# Revit family: Shower_Set-DXV-Modulus-D35120780_Series
name_source: partatom
category: Plumbing Fixtures
revit_build: Autodesk Revit 2018 (Build: 20170223_1515(x64)
units: mm (PartAtom-declared; Revit-internal decimal feet)

## family parameters
Cut with Voids When Loaded = No
Host = Face
OmniClass Number = 23.45.05.14.17
OmniClass Title = Showers
Part Type = Normal
Room Calculation Point = No
Round Connector Dimension = Use Diameter
Shared = Yes

## types (4) — shared parameters
Assembly Code = D2010710
CEC Compliant = Yes
CW Connection = Yes
CWFU = 3
CalGreen Compliant = Yes
Connection Size = 1/2"
Default Elevation = 0"
Description = DXV Modulus Personal Shower Set with Hand Shower
Flow Rate = 1.8 gpm (6.8 L/min)
HW Connection = Yes
HWFU = 3
Height = 23 5/8"
IAPMO Compliance = Meets or Exceeds ASME A112.18.1/CSA B125.1
Installation Type = Wall Mounted
Length = 3 7/16"
Manufacturer = DXV
Price = Prices may vary. Please consult Manufacturer Representative for most up-to-date price list.
Product Documentation Link = https://dxv01.blob.core.windows.net
Product Page URL = https://www.dxv.com
Revised Date = 04/07/2022
Type Comments = 5 ft. (1.5 m) decorative metal hose
URL = https://www.dxv.com
Vent Connection = No
WFU = 4
Wall Elbow Height From Floor = 48"
Wall Elbow Height From Floor Constraint = 48"
Waste Connection = No
Width = 2 1/4"

## per-type parameters (varying)
| type | Finish | Finish 2 | Material |
| D35120780.100 | Metal-DXV-100-Polished Chrome | Metal-DXV-150-Platinum Nickel | Metal-DXV-100-Polished Chrome |
| D35120780.144 | Metal-DXV-144-Brushed Nickel | Metal-DXV-150-Platinum Nickel | Metal-DXV-144-Brushed Nickel |
| D35120780.150 | Metal-DXV-150-Platinum Nickel | Metal-DXV-150-Platinum Nickel | Metal-DXV-150-Platinum Nickel |
| D35120780.243 | Metal-DXV-243-Matte Black | Metal-DXV-243-Matte Black | Metal-DXV-243-Matte Black |

note: column(s) folded — value = type name in every type: Model

## geometry (parser evidence)
native form markers: Sweep x2
no freeform markers — native parametric forms only
